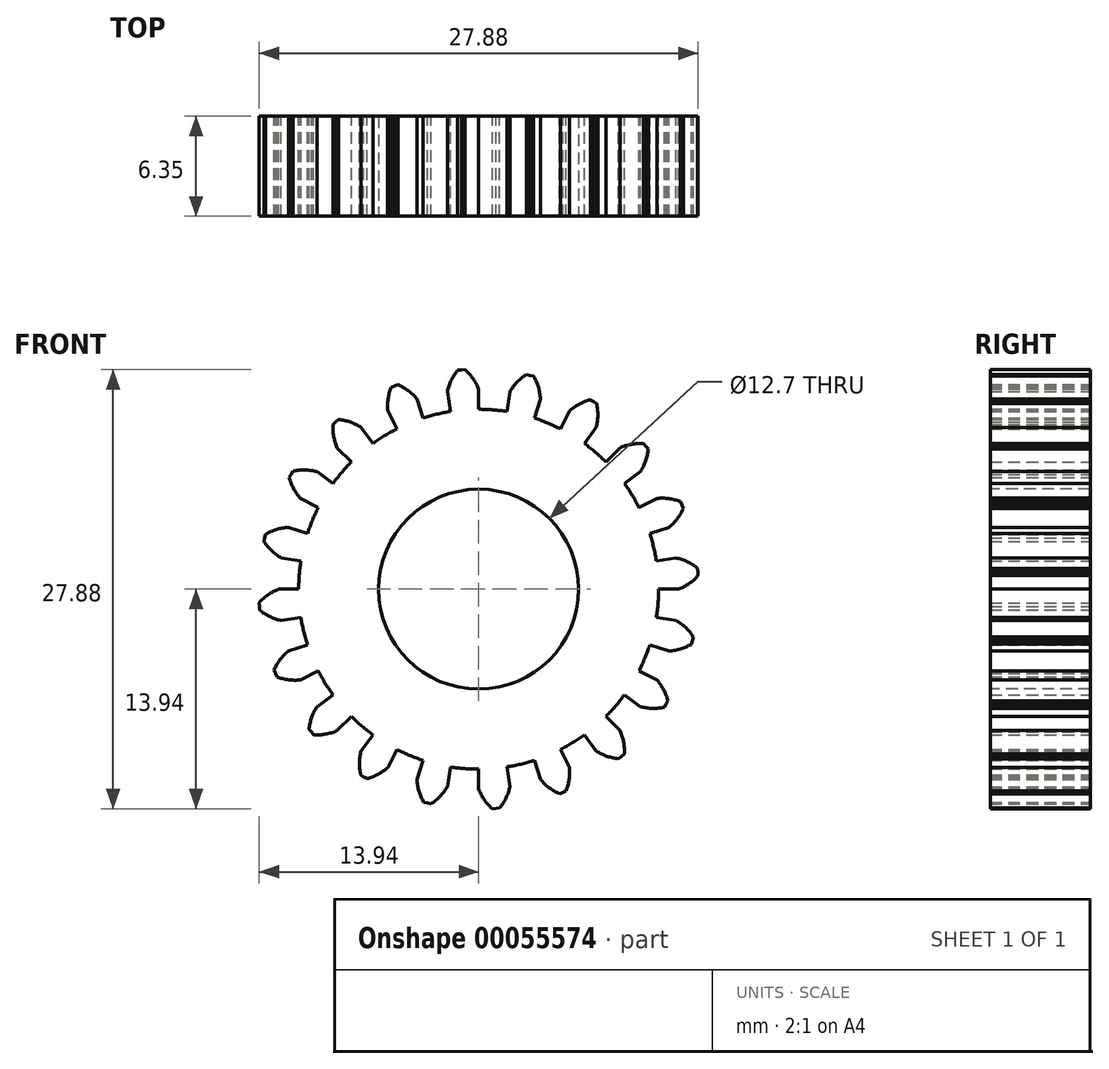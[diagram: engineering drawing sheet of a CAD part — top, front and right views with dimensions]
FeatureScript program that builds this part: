
annotation { "Feature Type Name" : "Feature", "Feature Type Description" : "" }
export const myFeature = defineFeature(function(context is Context, id is Id, definition is map)
    precondition{}
    {
        {
            var Q0;
            Q0=qCreatedBy(makeId("Front.planeOp"),FACE);
            var sketch = newSketch(context, id + "F0", { "sketchPlane" : qUnion([Q0])});
            skArc(sketch, "E0", {"start": v(-1.79, 11.29) * mm, "mid": v(-2.67, 11.11) * mm, "end": v(-3.53, 10.87) * mm});
            skArc(sketch, "E1.trimOffspring", {"start": v(0, 12.7) * mm, "mid": v(-0.36, 13.37) * mm, "end": v(-0.87, 13.94) * mm});
            skLineSegment(sketch, "E2", {"start": v(-0.87, 13.94) * mm, "end": v(-1.1, 13.93) * mm});
            skLineSegment(sketch, "E3.MirrorCS", {"start": v(-1.33, 13.9) * mm, "end": v(-1.1, 13.93) * mm});
            skArc(sketch, "E4.MirrorCS", {"start": v(-1.99, 12.54) * mm, "mid": v(-1.74, 13.27) * mm, "end": v(-1.33, 13.9) * mm});
            skLineSegment(sketch, "E5", {"start": v(0, 12.7) * mm, "end": v(0, 11.43) * mm});
            skLineSegment(sketch, "E6.MirrorCS", {"start": v(-1.99, 12.54) * mm, "end": v(-1.79, 11.29) * mm});
            skLineSegment(sketch, "E7.1.0", {"start": v(-5.13, 13) * mm, "end": v(-5.35, 12.9) * mm});
            skLineSegment(sketch, "E7.1.1", {"start": v(-5.56, 12.82) * mm, "end": v(-5.35, 12.9) * mm});
            skArc(sketch, "E7.1.2", {"start": v(-5.77, 11.32) * mm, "mid": v(-5.75, 12.08) * mm, "end": v(-5.56, 12.82) * mm});
            skArc(sketch, "E7.1.3", {"start": v(-3.92, 12.08) * mm, "mid": v(-4.47, 12.6) * mm, "end": v(-5.13, 13) * mm});
            skLineSegment(sketch, "E7.1.4", {"start": v(-3.92, 12.08) * mm, "end": v(-3.53, 10.87) * mm});
            skLineSegment(sketch, "E7.1.5", {"start": v(-5.77, 11.32) * mm, "end": v(-5.19, 10.18) * mm});
            skLineSegment(sketch, "E7.2.0", {"start": v(-8.9, 10.77) * mm, "end": v(-9.07, 10.62) * mm});
            skLineSegment(sketch, "E7.2.1", {"start": v(-9.25, 10.47) * mm, "end": v(-9.07, 10.62) * mm});
            skArc(sketch, "E7.2.2", {"start": v(-8.98, 8.98) * mm, "mid": v(-9.2, 9.7) * mm, "end": v(-9.25, 10.47) * mm});
            skArc(sketch, "E7.2.3", {"start": v(-7.46, 10.27) * mm, "mid": v(-8.15, 10.6) * mm, "end": v(-8.9, 10.77) * mm});
            skLineSegment(sketch, "E7.2.4", {"start": v(-7.46, 10.27) * mm, "end": v(-6.72, 9.25) * mm});
            skLineSegment(sketch, "E7.2.5", {"start": v(-8.98, 8.98) * mm, "end": v(-8.08, 8.08) * mm});
            skLineSegment(sketch, "E7.3.0", {"start": v(-11.79, 7.5) * mm, "end": v(-11.91, 7.3) * mm});
            skLineSegment(sketch, "E7.3.1", {"start": v(-12.03, 7.1) * mm, "end": v(-11.91, 7.3) * mm});
            skArc(sketch, "E7.3.2", {"start": v(-11.32, 5.77) * mm, "mid": v(-11.75, 6.4) * mm, "end": v(-12.03, 7.1) * mm});
            skArc(sketch, "E7.3.3", {"start": v(-10.27, 7.46) * mm, "mid": v(-11.03, 7.57) * mm, "end": v(-11.79, 7.5) * mm});
            skLineSegment(sketch, "E7.3.4", {"start": v(-10.27, 7.46) * mm, "end": v(-9.25, 6.72) * mm});
            skLineSegment(sketch, "E7.3.5", {"start": v(-11.32, 5.77) * mm, "end": v(-10.18, 5.19) * mm});
            skLineSegment(sketch, "E7.4.0", {"start": v(-13.53, 3.49) * mm, "end": v(-13.59, 3.26) * mm});
            skLineSegment(sketch, "E7.4.1", {"start": v(-13.64, 3.04) * mm, "end": v(-13.59, 3.26) * mm});
            skArc(sketch, "E7.4.2", {"start": v(-12.54, 1.99) * mm, "mid": v(-13.15, 2.45) * mm, "end": v(-13.64, 3.04) * mm});
            skArc(sketch, "E7.4.3", {"start": v(-12.08, 3.92) * mm, "mid": v(-12.83, 3.8) * mm, "end": v(-13.53, 3.49) * mm});
            skLineSegment(sketch, "E7.4.4", {"start": v(-12.08, 3.92) * mm, "end": v(-10.87, 3.53) * mm});
            skLineSegment(sketch, "E7.4.5", {"start": v(-12.54, 1.99) * mm, "end": v(-11.29, 1.79) * mm});
            skLineSegment(sketch, "E7.5.0", {"start": v(-13.94, -0.87) * mm, "end": v(-13.93, -1.1) * mm});
            skLineSegment(sketch, "E7.5.1", {"start": v(-13.9, -1.33) * mm, "end": v(-13.93, -1.1) * mm});
            skArc(sketch, "E7.5.2", {"start": v(-12.54, -1.99) * mm, "mid": v(-13.27, -1.74) * mm, "end": v(-13.9, -1.33) * mm});
            skArc(sketch, "E7.5.3", {"start": v(-12.7, 0) * mm, "mid": v(-13.37, -0.36) * mm, "end": v(-13.94, -0.87) * mm});
            skLineSegment(sketch, "E7.5.4", {"start": v(-12.7, 0) * mm, "end": v(-11.43, 0) * mm});
            skLineSegment(sketch, "E7.5.5", {"start": v(-12.54, -1.99) * mm, "end": v(-11.29, -1.79) * mm});
            skLineSegment(sketch, "E7.6.0", {"start": v(-13, -5.13) * mm, "end": v(-12.9, -5.35) * mm});
            skLineSegment(sketch, "E7.6.1", {"start": v(-12.82, -5.56) * mm, "end": v(-12.9, -5.35) * mm});
            skArc(sketch, "E7.6.2", {"start": v(-11.32, -5.77) * mm, "mid": v(-12.08, -5.75) * mm, "end": v(-12.82, -5.56) * mm});
            skArc(sketch, "E7.6.3", {"start": v(-12.08, -3.92) * mm, "mid": v(-12.6, -4.47) * mm, "end": v(-13, -5.13) * mm});
            skLineSegment(sketch, "E7.6.4", {"start": v(-12.08, -3.92) * mm, "end": v(-10.87, -3.53) * mm});
            skLineSegment(sketch, "E7.6.5", {"start": v(-11.32, -5.77) * mm, "end": v(-10.18, -5.19) * mm});
            skLineSegment(sketch, "E7.7.0", {"start": v(-10.77, -8.9) * mm, "end": v(-10.62, -9.07) * mm});
            skLineSegment(sketch, "E7.7.1", {"start": v(-10.47, -9.25) * mm, "end": v(-10.62, -9.07) * mm});
            skArc(sketch, "E7.7.2", {"start": v(-8.98, -8.98) * mm, "mid": v(-9.7, -9.2) * mm, "end": v(-10.47, -9.25) * mm});
            skArc(sketch, "E7.7.3", {"start": v(-10.27, -7.46) * mm, "mid": v(-10.6, -8.15) * mm, "end": v(-10.77, -8.9) * mm});
            skLineSegment(sketch, "E7.7.4", {"start": v(-10.27, -7.46) * mm, "end": v(-9.25, -6.72) * mm});
            skLineSegment(sketch, "E7.7.5", {"start": v(-8.98, -8.98) * mm, "end": v(-8.08, -8.08) * mm});
            skLineSegment(sketch, "E7.8.0", {"start": v(-7.5, -11.79) * mm, "end": v(-7.3, -11.91) * mm});
            skLineSegment(sketch, "E7.8.1", {"start": v(-7.1, -12.03) * mm, "end": v(-7.3, -11.91) * mm});
            skArc(sketch, "E7.8.2", {"start": v(-5.77, -11.32) * mm, "mid": v(-6.4, -11.75) * mm, "end": v(-7.1, -12.03) * mm});
            skArc(sketch, "E7.8.3", {"start": v(-7.46, -10.27) * mm, "mid": v(-7.57, -11.03) * mm, "end": v(-7.5, -11.79) * mm});
            skLineSegment(sketch, "E7.8.4", {"start": v(-7.46, -10.27) * mm, "end": v(-6.72, -9.25) * mm});
            skLineSegment(sketch, "E7.8.5", {"start": v(-5.77, -11.32) * mm, "end": v(-5.19, -10.18) * mm});
            skLineSegment(sketch, "E7.9.0", {"start": v(-3.49, -13.53) * mm, "end": v(-3.26, -13.59) * mm});
            skLineSegment(sketch, "E7.9.1", {"start": v(-3.04, -13.64) * mm, "end": v(-3.26, -13.59) * mm});
            skArc(sketch, "E7.9.2", {"start": v(-1.99, -12.54) * mm, "mid": v(-2.45, -13.15) * mm, "end": v(-3.04, -13.64) * mm});
            skArc(sketch, "E7.9.3", {"start": v(-3.92, -12.08) * mm, "mid": v(-3.8, -12.83) * mm, "end": v(-3.49, -13.53) * mm});
            skLineSegment(sketch, "E7.9.4", {"start": v(-3.92, -12.08) * mm, "end": v(-3.53, -10.87) * mm});
            skLineSegment(sketch, "E7.9.5", {"start": v(-1.99, -12.54) * mm, "end": v(-1.79, -11.29) * mm});
            skLineSegment(sketch, "E7.10.0", {"start": v(0.87, -13.94) * mm, "end": v(1.1, -13.93) * mm});
            skLineSegment(sketch, "E7.10.1", {"start": v(1.33, -13.9) * mm, "end": v(1.1, -13.93) * mm});
            skArc(sketch, "E7.10.2", {"start": v(1.99, -12.54) * mm, "mid": v(1.74, -13.27) * mm, "end": v(1.33, -13.9) * mm});
            skArc(sketch, "E7.10.3", {"start": v(0, -12.7) * mm, "mid": v(0.36, -13.37) * mm, "end": v(0.87, -13.94) * mm});
            skLineSegment(sketch, "E7.10.4", {"start": v(0, -12.7) * mm, "end": v(0, -11.43) * mm});
            skLineSegment(sketch, "E7.10.5", {"start": v(1.99, -12.54) * mm, "end": v(1.79, -11.29) * mm});
            skLineSegment(sketch, "E7.11.0", {"start": v(5.13, -13) * mm, "end": v(5.35, -12.9) * mm});
            skLineSegment(sketch, "E7.11.1", {"start": v(5.56, -12.82) * mm, "end": v(5.35, -12.9) * mm});
            skArc(sketch, "E7.11.2", {"start": v(5.77, -11.32) * mm, "mid": v(5.75, -12.08) * mm, "end": v(5.56, -12.82) * mm});
            skArc(sketch, "E7.11.3", {"start": v(3.92, -12.08) * mm, "mid": v(4.47, -12.6) * mm, "end": v(5.13, -13) * mm});
            skLineSegment(sketch, "E7.11.4", {"start": v(3.92, -12.08) * mm, "end": v(3.53, -10.87) * mm});
            skLineSegment(sketch, "E7.11.5", {"start": v(5.77, -11.32) * mm, "end": v(5.19, -10.18) * mm});
            skLineSegment(sketch, "E7.12.0", {"start": v(8.9, -10.77) * mm, "end": v(9.07, -10.62) * mm});
            skLineSegment(sketch, "E7.12.1", {"start": v(9.25, -10.47) * mm, "end": v(9.07, -10.62) * mm});
            skArc(sketch, "E7.12.2", {"start": v(8.98, -8.98) * mm, "mid": v(9.2, -9.7) * mm, "end": v(9.25, -10.47) * mm});
            skArc(sketch, "E7.12.3", {"start": v(7.46, -10.27) * mm, "mid": v(8.15, -10.6) * mm, "end": v(8.9, -10.77) * mm});
            skLineSegment(sketch, "E7.12.4", {"start": v(7.46, -10.27) * mm, "end": v(6.72, -9.25) * mm});
            skLineSegment(sketch, "E7.12.5", {"start": v(8.98, -8.98) * mm, "end": v(8.08, -8.08) * mm});
            skLineSegment(sketch, "E7.13.0", {"start": v(11.79, -7.5) * mm, "end": v(11.91, -7.3) * mm});
            skLineSegment(sketch, "E7.13.1", {"start": v(12.03, -7.1) * mm, "end": v(11.91, -7.3) * mm});
            skArc(sketch, "E7.13.2", {"start": v(11.32, -5.77) * mm, "mid": v(11.75, -6.4) * mm, "end": v(12.03, -7.1) * mm});
            skArc(sketch, "E7.13.3", {"start": v(10.27, -7.46) * mm, "mid": v(11.03, -7.57) * mm, "end": v(11.79, -7.5) * mm});
            skLineSegment(sketch, "E7.13.4", {"start": v(10.27, -7.46) * mm, "end": v(9.25, -6.72) * mm});
            skLineSegment(sketch, "E7.13.5", {"start": v(11.32, -5.77) * mm, "end": v(10.18, -5.19) * mm});
            skLineSegment(sketch, "E7.14.0", {"start": v(13.53, -3.49) * mm, "end": v(13.59, -3.26) * mm});
            skLineSegment(sketch, "E7.14.1", {"start": v(13.64, -3.04) * mm, "end": v(13.59, -3.26) * mm});
            skArc(sketch, "E7.14.2", {"start": v(12.54, -1.99) * mm, "mid": v(13.15, -2.45) * mm, "end": v(13.64, -3.04) * mm});
            skArc(sketch, "E7.14.3", {"start": v(12.08, -3.92) * mm, "mid": v(12.83, -3.8) * mm, "end": v(13.53, -3.49) * mm});
            skLineSegment(sketch, "E7.14.4", {"start": v(12.08, -3.92) * mm, "end": v(10.87, -3.53) * mm});
            skLineSegment(sketch, "E7.14.5", {"start": v(12.54, -1.99) * mm, "end": v(11.29, -1.79) * mm});
            skLineSegment(sketch, "E7.15.0", {"start": v(13.94, 0.87) * mm, "end": v(13.93, 1.1) * mm});
            skLineSegment(sketch, "E7.15.1", {"start": v(13.9, 1.33) * mm, "end": v(13.93, 1.1) * mm});
            skArc(sketch, "E7.15.2", {"start": v(12.54, 1.99) * mm, "mid": v(13.27, 1.74) * mm, "end": v(13.9, 1.33) * mm});
            skArc(sketch, "E7.15.3", {"start": v(12.7, 0) * mm, "mid": v(13.37, 0.36) * mm, "end": v(13.94, 0.87) * mm});
            skLineSegment(sketch, "E7.15.4", {"start": v(12.7, 0) * mm, "end": v(11.43, 0) * mm});
            skLineSegment(sketch, "E7.15.5", {"start": v(12.54, 1.99) * mm, "end": v(11.29, 1.79) * mm});
            skLineSegment(sketch, "E7.16.0", {"start": v(13, 5.13) * mm, "end": v(12.9, 5.35) * mm});
            skLineSegment(sketch, "E7.16.1", {"start": v(12.82, 5.56) * mm, "end": v(12.9, 5.35) * mm});
            skArc(sketch, "E7.16.2", {"start": v(11.32, 5.77) * mm, "mid": v(12.08, 5.75) * mm, "end": v(12.82, 5.56) * mm});
            skArc(sketch, "E7.16.3", {"start": v(12.08, 3.92) * mm, "mid": v(12.6, 4.47) * mm, "end": v(13, 5.13) * mm});
            skLineSegment(sketch, "E7.16.4", {"start": v(12.08, 3.92) * mm, "end": v(10.87, 3.53) * mm});
            skLineSegment(sketch, "E7.16.5", {"start": v(11.32, 5.77) * mm, "end": v(10.18, 5.19) * mm});
            skLineSegment(sketch, "E7.17.0", {"start": v(10.77, 8.9) * mm, "end": v(10.62, 9.07) * mm});
            skLineSegment(sketch, "E7.17.1", {"start": v(10.47, 9.25) * mm, "end": v(10.62, 9.07) * mm});
            skArc(sketch, "E7.17.2", {"start": v(8.98, 8.98) * mm, "mid": v(9.7, 9.2) * mm, "end": v(10.47, 9.25) * mm});
            skArc(sketch, "E7.17.3", {"start": v(10.27, 7.46) * mm, "mid": v(10.6, 8.15) * mm, "end": v(10.77, 8.9) * mm});
            skLineSegment(sketch, "E7.17.4", {"start": v(10.27, 7.46) * mm, "end": v(9.25, 6.72) * mm});
            skLineSegment(sketch, "E7.17.5", {"start": v(8.98, 8.98) * mm, "end": v(8.08, 8.08) * mm});
            skLineSegment(sketch, "E7.18.0", {"start": v(7.5, 11.79) * mm, "end": v(7.3, 11.91) * mm});
            skLineSegment(sketch, "E7.18.1", {"start": v(7.1, 12.03) * mm, "end": v(7.3, 11.91) * mm});
            skArc(sketch, "E7.18.2", {"start": v(5.77, 11.32) * mm, "mid": v(6.4, 11.75) * mm, "end": v(7.1, 12.03) * mm});
            skArc(sketch, "E7.18.3", {"start": v(7.46, 10.27) * mm, "mid": v(7.57, 11.03) * mm, "end": v(7.5, 11.79) * mm});
            skLineSegment(sketch, "E7.18.4", {"start": v(7.46, 10.27) * mm, "end": v(6.72, 9.25) * mm});
            skLineSegment(sketch, "E7.18.5", {"start": v(5.77, 11.32) * mm, "end": v(5.19, 10.18) * mm});
            skLineSegment(sketch, "E7.19.0", {"start": v(3.49, 13.53) * mm, "end": v(3.26, 13.59) * mm});
            skLineSegment(sketch, "E7.19.1", {"start": v(3.04, 13.64) * mm, "end": v(3.26, 13.59) * mm});
            skArc(sketch, "E7.19.2", {"start": v(1.99, 12.54) * mm, "mid": v(2.45, 13.15) * mm, "end": v(3.04, 13.64) * mm});
            skArc(sketch, "E7.19.3", {"start": v(3.92, 12.08) * mm, "mid": v(3.8, 12.83) * mm, "end": v(3.49, 13.53) * mm});
            skLineSegment(sketch, "E7.19.4", {"start": v(3.92, 12.08) * mm, "end": v(3.53, 10.87) * mm});
            skLineSegment(sketch, "E7.19.5", {"start": v(1.99, 12.54) * mm, "end": v(1.79, 11.29) * mm});
            skArc(sketch, "E8.trimOffspring", {"start": v(1.79, 11.29) * mm, "mid": v(0.9, 11.4) * mm, "end": v(0, 11.43) * mm});
            skArc(sketch, "E9.trimOffspring", {"start": v(5.19, 10.18) * mm, "mid": v(4.37, 10.56) * mm, "end": v(3.53, 10.87) * mm});
            skArc(sketch, "E10.trimOffspring", {"start": v(8.08, 8.08) * mm, "mid": v(7.42, 8.7) * mm, "end": v(6.72, 9.25) * mm});
            skArc(sketch, "E11.trimOffspring", {"start": v(10.18, 5.19) * mm, "mid": v(9.75, 5.97) * mm, "end": v(9.25, 6.72) * mm});
            skArc(sketch, "E12.trimOffspring", {"start": v(11.29, 1.79) * mm, "mid": v(11.11, 2.67) * mm, "end": v(10.87, 3.53) * mm});
            skArc(sketch, "E13.trimOffspring", {"start": v(11.29, -1.79) * mm, "mid": v(11.4, -0.9) * mm, "end": v(11.43, 0) * mm});
            skArc(sketch, "E14.trimOffspring", {"start": v(10.18, -5.19) * mm, "mid": v(10.56, -4.37) * mm, "end": v(10.87, -3.53) * mm});
            skArc(sketch, "E15.trimOffspring", {"start": v(8.08, -8.08) * mm, "mid": v(8.7, -7.42) * mm, "end": v(9.25, -6.72) * mm});
            skArc(sketch, "E16.trimOffspring", {"start": v(5.19, -10.18) * mm, "mid": v(5.97, -9.75) * mm, "end": v(6.72, -9.25) * mm});
            skArc(sketch, "E17.trimOffspring", {"start": v(1.79, -11.29) * mm, "mid": v(2.67, -11.11) * mm, "end": v(3.53, -10.87) * mm});
            skArc(sketch, "E18.trimOffspring", {"start": v(-1.79, -11.29) * mm, "mid": v(-0.9, -11.4) * mm, "end": v(0, -11.43) * mm});
            skArc(sketch, "E19.trimOffspring", {"start": v(-5.19, -10.18) * mm, "mid": v(-4.37, -10.56) * mm, "end": v(-3.53, -10.87) * mm});
            skArc(sketch, "E20.trimOffspring", {"start": v(-8.08, -8.08) * mm, "mid": v(-7.42, -8.7) * mm, "end": v(-6.72, -9.25) * mm});
            skArc(sketch, "E21.trimOffspring", {"start": v(-10.18, -5.19) * mm, "mid": v(-9.75, -5.97) * mm, "end": v(-9.25, -6.72) * mm});
            skArc(sketch, "E22.trimOffspring", {"start": v(-11.29, -1.79) * mm, "mid": v(-11.11, -2.67) * mm, "end": v(-10.87, -3.53) * mm});
            skArc(sketch, "E23.trimOffspring", {"start": v(-11.29, 1.79) * mm, "mid": v(-11.4, 0.9) * mm, "end": v(-11.43, 0) * mm});
            skArc(sketch, "E24.trimOffspring", {"start": v(-10.18, 5.19) * mm, "mid": v(-10.56, 4.37) * mm, "end": v(-10.87, 3.53) * mm});
            skArc(sketch, "E25.trimOffspring", {"start": v(-8.08, 8.08) * mm, "mid": v(-8.7, 7.42) * mm, "end": v(-9.25, 6.72) * mm});
            skArc(sketch, "E26.trimOffspring", {"start": v(-5.19, 10.18) * mm, "mid": v(-5.97, 9.75) * mm, "end": v(-6.72, 9.25) * mm});
            skSolve(sketch);
        }
        {
            var Q0;
            Q0 = qSketchRegion(id + "F0", true);
            extrude(context, id + "F1", {"entities" : qUnion([Q0]), "depth" : 6.35 * mm});
        }
        {
            var Q0;
            Q0=makeQuery(id+"F1.opExtrude","CAP_FACE",FACE,{"disambiguationData":[OSD([sQuery(id+"F0.wireOp",EDGE,"E0"),sQuery(id+"F0.wireOp",EDGE,"E1.trimOffspring"),sQuery(id+"F0.wireOp",EDGE,"E2"),sQuery(id+"F0.wireOp",EDGE,"E3.MirrorCS"),sQuery(id+"F0.wireOp",EDGE,"E4.MirrorCS"),sQuery(id+"F0.wireOp",EDGE,"E5"),sQuery(id+"F0.wireOp",EDGE,"E6.MirrorCS"),sQuery(id+"F0.wireOp",EDGE,"E7.1.0"),sQuery(id+"F0.wireOp",EDGE,"E7.1.1"),sQuery(id+"F0.wireOp",EDGE,"E7.1.2"),sQuery(id+"F0.wireOp",EDGE,"E7.1.3"),sQuery(id+"F0.wireOp",EDGE,"E7.1.4"),sQuery(id+"F0.wireOp",EDGE,"E7.1.5"),sQuery(id+"F0.wireOp",EDGE,"E7.2.0"),sQuery(id+"F0.wireOp",EDGE,"E7.2.1"),sQuery(id+"F0.wireOp",EDGE,"E7.2.2"),sQuery(id+"F0.wireOp",EDGE,"E7.2.3"),sQuery(id+"F0.wireOp",EDGE,"E7.2.4"),sQuery(id+"F0.wireOp",EDGE,"E7.2.5"),sQuery(id+"F0.wireOp",EDGE,"E7.3.0"),sQuery(id+"F0.wireOp",EDGE,"E7.3.1"),sQuery(id+"F0.wireOp",EDGE,"E7.3.2"),sQuery(id+"F0.wireOp",EDGE,"E7.3.3"),sQuery(id+"F0.wireOp",EDGE,"E7.3.4"),sQuery(id+"F0.wireOp",EDGE,"E7.3.5"),sQuery(id+"F0.wireOp",EDGE,"E7.4.0"),sQuery(id+"F0.wireOp",EDGE,"E7.4.1"),sQuery(id+"F0.wireOp",EDGE,"E7.4.2"),sQuery(id+"F0.wireOp",EDGE,"E7.4.3"),sQuery(id+"F0.wireOp",EDGE,"E7.4.4"),sQuery(id+"F0.wireOp",EDGE,"E7.4.5"),sQuery(id+"F0.wireOp",EDGE,"E7.5.0"),sQuery(id+"F0.wireOp",EDGE,"E7.5.1"),sQuery(id+"F0.wireOp",EDGE,"E7.5.2"),sQuery(id+"F0.wireOp",EDGE,"E7.5.3"),sQuery(id+"F0.wireOp",EDGE,"E7.5.4"),sQuery(id+"F0.wireOp",EDGE,"E7.5.5"),sQuery(id+"F0.wireOp",EDGE,"E7.6.0"),sQuery(id+"F0.wireOp",EDGE,"E7.6.1"),sQuery(id+"F0.wireOp",EDGE,"E7.6.2"),sQuery(id+"F0.wireOp",EDGE,"E7.6.3"),sQuery(id+"F0.wireOp",EDGE,"E7.6.4"),sQuery(id+"F0.wireOp",EDGE,"E7.6.5"),sQuery(id+"F0.wireOp",EDGE,"E7.7.0"),sQuery(id+"F0.wireOp",EDGE,"E7.7.1"),sQuery(id+"F0.wireOp",EDGE,"E7.7.2"),sQuery(id+"F0.wireOp",EDGE,"E7.7.3"),sQuery(id+"F0.wireOp",EDGE,"E7.7.4"),sQuery(id+"F0.wireOp",EDGE,"E7.7.5"),sQuery(id+"F0.wireOp",EDGE,"E7.8.0"),sQuery(id+"F0.wireOp",EDGE,"E7.8.1"),sQuery(id+"F0.wireOp",EDGE,"E7.8.2"),sQuery(id+"F0.wireOp",EDGE,"E7.8.3"),sQuery(id+"F0.wireOp",EDGE,"E7.8.4"),sQuery(id+"F0.wireOp",EDGE,"E7.8.5"),sQuery(id+"F0.wireOp",EDGE,"E7.9.0"),sQuery(id+"F0.wireOp",EDGE,"E7.9.1"),sQuery(id+"F0.wireOp",EDGE,"E7.9.2"),sQuery(id+"F0.wireOp",EDGE,"E7.9.3"),sQuery(id+"F0.wireOp",EDGE,"E7.9.4"),sQuery(id+"F0.wireOp",EDGE,"E7.9.5"),sQuery(id+"F0.wireOp",EDGE,"E7.10.0"),sQuery(id+"F0.wireOp",EDGE,"E7.10.1"),sQuery(id+"F0.wireOp",EDGE,"E7.10.2"),sQuery(id+"F0.wireOp",EDGE,"E7.10.3"),sQuery(id+"F0.wireOp",EDGE,"E7.10.4"),sQuery(id+"F0.wireOp",EDGE,"E7.10.5"),sQuery(id+"F0.wireOp",EDGE,"E7.11.0"),sQuery(id+"F0.wireOp",EDGE,"E7.11.1"),sQuery(id+"F0.wireOp",EDGE,"E7.11.2"),sQuery(id+"F0.wireOp",EDGE,"E7.11.3"),sQuery(id+"F0.wireOp",EDGE,"E7.11.4"),sQuery(id+"F0.wireOp",EDGE,"E7.11.5"),sQuery(id+"F0.wireOp",EDGE,"E7.12.0"),sQuery(id+"F0.wireOp",EDGE,"E7.12.1"),sQuery(id+"F0.wireOp",EDGE,"E7.12.2"),sQuery(id+"F0.wireOp",EDGE,"E7.12.3"),sQuery(id+"F0.wireOp",EDGE,"E7.12.4"),sQuery(id+"F0.wireOp",EDGE,"E7.12.5"),sQuery(id+"F0.wireOp",EDGE,"E7.13.0"),sQuery(id+"F0.wireOp",EDGE,"E7.13.1"),sQuery(id+"F0.wireOp",EDGE,"E7.13.2"),sQuery(id+"F0.wireOp",EDGE,"E7.13.3"),sQuery(id+"F0.wireOp",EDGE,"E7.13.4"),sQuery(id+"F0.wireOp",EDGE,"E7.13.5"),sQuery(id+"F0.wireOp",EDGE,"E7.14.0"),sQuery(id+"F0.wireOp",EDGE,"E7.14.1"),sQuery(id+"F0.wireOp",EDGE,"E7.14.2"),sQuery(id+"F0.wireOp",EDGE,"E7.14.3"),sQuery(id+"F0.wireOp",EDGE,"E7.14.4"),sQuery(id+"F0.wireOp",EDGE,"E7.14.5"),sQuery(id+"F0.wireOp",EDGE,"E7.15.0"),sQuery(id+"F0.wireOp",EDGE,"E7.15.1"),sQuery(id+"F0.wireOp",EDGE,"E7.15.2"),sQuery(id+"F0.wireOp",EDGE,"E7.15.3"),sQuery(id+"F0.wireOp",EDGE,"E7.15.4"),sQuery(id+"F0.wireOp",EDGE,"E7.15.5"),sQuery(id+"F0.wireOp",EDGE,"E7.16.0"),sQuery(id+"F0.wireOp",EDGE,"E7.16.1"),sQuery(id+"F0.wireOp",EDGE,"E7.16.2"),sQuery(id+"F0.wireOp",EDGE,"E7.16.3"),sQuery(id+"F0.wireOp",EDGE,"E7.16.4"),sQuery(id+"F0.wireOp",EDGE,"E7.16.5"),sQuery(id+"F0.wireOp",EDGE,"E7.17.0"),sQuery(id+"F0.wireOp",EDGE,"E7.17.1"),sQuery(id+"F0.wireOp",EDGE,"E7.17.2"),sQuery(id+"F0.wireOp",EDGE,"E7.17.3"),sQuery(id+"F0.wireOp",EDGE,"E7.17.4"),sQuery(id+"F0.wireOp",EDGE,"E7.17.5"),sQuery(id+"F0.wireOp",EDGE,"E7.18.0"),sQuery(id+"F0.wireOp",EDGE,"E7.18.1"),sQuery(id+"F0.wireOp",EDGE,"E7.18.2"),sQuery(id+"F0.wireOp",EDGE,"E7.18.3"),sQuery(id+"F0.wireOp",EDGE,"E7.18.4"),sQuery(id+"F0.wireOp",EDGE,"E7.18.5"),sQuery(id+"F0.wireOp",EDGE,"E7.19.0"),sQuery(id+"F0.wireOp",EDGE,"E7.19.1"),sQuery(id+"F0.wireOp",EDGE,"E7.19.2"),sQuery(id+"F0.wireOp",EDGE,"E7.19.3"),sQuery(id+"F0.wireOp",EDGE,"E7.19.4"),sQuery(id+"F0.wireOp",EDGE,"E7.19.5"),sQuery(id+"F0.wireOp",EDGE,"E8.trimOffspring"),sQuery(id+"F0.wireOp",EDGE,"E9.trimOffspring"),sQuery(id+"F0.wireOp",EDGE,"E10.trimOffspring"),sQuery(id+"F0.wireOp",EDGE,"E11.trimOffspring"),sQuery(id+"F0.wireOp",EDGE,"E12.trimOffspring"),sQuery(id+"F0.wireOp",EDGE,"E13.trimOffspring"),sQuery(id+"F0.wireOp",EDGE,"E14.trimOffspring"),sQuery(id+"F0.wireOp",EDGE,"E15.trimOffspring"),sQuery(id+"F0.wireOp",EDGE,"E16.trimOffspring"),sQuery(id+"F0.wireOp",EDGE,"E17.trimOffspring"),sQuery(id+"F0.wireOp",EDGE,"E18.trimOffspring"),sQuery(id+"F0.wireOp",EDGE,"E19.trimOffspring"),sQuery(id+"F0.wireOp",EDGE,"E20.trimOffspring"),sQuery(id+"F0.wireOp",EDGE,"E21.trimOffspring"),sQuery(id+"F0.wireOp",EDGE,"E22.trimOffspring"),sQuery(id+"F0.wireOp",EDGE,"E23.trimOffspring"),sQuery(id+"F0.wireOp",EDGE,"E24.trimOffspring"),sQuery(id+"F0.wireOp",EDGE,"E25.trimOffspring"),sQuery(id+"F0.wireOp",EDGE,"E26.trimOffspring")])],"isStart":false});
            var sketch = newSketch(context, id + "F2", { "sketchPlane" : qUnion([Q0])});
            skCircle(sketch, "E27", {"center": v(0, 0) * mm, "radius": 6.35 * mm});
            skSolve(sketch);
        }
        {
            var Q0;
            Q0=makeQuery(id+"F2.imprint","IMPRINT",FACE,{"disambiguationData":[TD([[makeQuery(id+"F2.imprint","IMPRINT",EDGE,{"derivedFrom":sQuery(id+"F2.wireOp",EDGE,"E27")}),1.0]])]});
            extrude(context, id + "F3", {"entities" : qUnion([Q0]), "operationType" : NewBodyOperationType.REMOVE, "oppositeDirection" : true, "depth" : 25.4 * mm});
        }
    });
